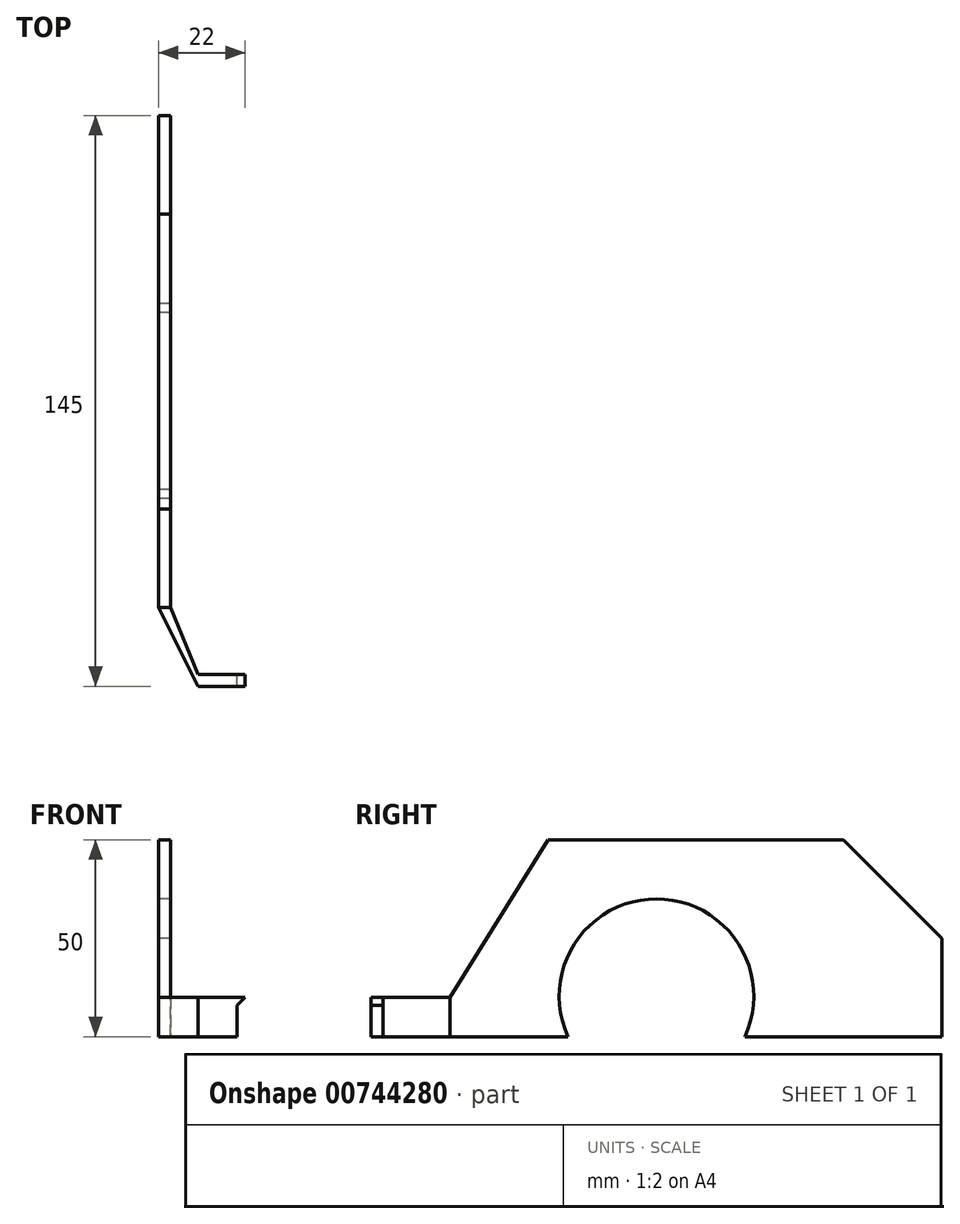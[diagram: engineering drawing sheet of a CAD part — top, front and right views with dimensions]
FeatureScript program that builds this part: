
annotation { "Feature Type Name" : "Feature", "Feature Type Description" : "" }
export const myFeature = defineFeature(function(context is Context, id is Id, definition is map)
    precondition{}
    {
        {
            var Q0;
            Q0=qCreatedBy(makeId("Top.planeOp"),FACE);
            var sketch = newSketch(context, id + "F0", { "sketchPlane" : qUnion([Q0])});
            skLineSegment(sketch, "E0", {"start": v(0, 0) * mm, "end": v(0, 3) * mm});
            skLineSegment(sketch, "E1", {"start": v(0, 3) * mm, "end": v(10, 3) * mm});
            skLineSegment(sketch, "E2", {"start": v(10, 3) * mm, "end": v(17, 20) * mm});
            skLineSegment(sketch, "E3", {"start": v(17, 20) * mm, "end": v(17, 145) * mm});
            skLineSegment(sketch, "E4", {"start": v(17, 145) * mm, "end": v(20, 145) * mm});
            skLineSegment(sketch, "E5", {"start": v(20, 145) * mm, "end": v(20, 20) * mm});
            skLineSegment(sketch, "E6", {"start": v(20, 20) * mm, "end": v(10, 0) * mm});
            skLineSegment(sketch, "E7", {"start": v(10, 0) * mm, "end": v(0, 0) * mm});
            skSolve(sketch);
        }
        {
            var Q0;
            Q0=makeQuery(id+"F0.imprint","IMPRINT",FACE,{"disambiguationData":[TD([[makeQuery(id+"F0.imprint","IMPRINT",EDGE,{"derivedFrom":sQuery(id+"F0.wireOp",EDGE,"E0")}),-1.0]])]});
            extrude(context, id + "F1", {"entities" : qUnion([Q0]), "depth" : 10 * mm, "offsetDistance" : 25 * mm});
        }
        {
            var Q0;
            Q0=qCreatedBy(makeId("Front.planeOp"),FACE);
            var sketch = newSketch(context, id + "F2", { "sketchPlane" : qUnion([Q0])});
            skLineSegment(sketch, "E8", {"start": v(0, 10) * mm, "end": v(-2, 10) * mm});
            skLineSegment(sketch, "E9", {"start": v(-2, 10) * mm, "end": v(0, 8) * mm});
            skLineSegment(sketch, "E10", {"start": v(0, 8) * mm, "end": v(0, 10) * mm});
            skSolve(sketch);
        }
        {
            var Q0;
            Q0=qSketchRegion(id+"F2",true);
            extrude(context, id + "F3", {"entities" : qUnion([Q0]), "operationType" : NewBodyOperationType.ADD, "oppositeDirection" : true, "depth" : 3 * mm, "offsetDistance" : 25 * mm});
        }
        {
            var Q0;
            Q0=makeQuery(id+"F3.boolean.opBoolean","MERGE",FACE,{"derivedFrom":[makeQuery(id+"F1.opExtrude","CAP_FACE",FACE,{"disambiguationData":[OSD([sQuery(id+"F0.wireOp",EDGE,"E0"),sQuery(id+"F0.wireOp",EDGE,"E1"),sQuery(id+"F0.wireOp",EDGE,"E2"),sQuery(id+"F0.wireOp",EDGE,"E3"),sQuery(id+"F0.wireOp",EDGE,"E4"),sQuery(id+"F0.wireOp",EDGE,"E5"),sQuery(id+"F0.wireOp",EDGE,"E6"),sQuery(id+"F0.wireOp",EDGE,"E7")])],"isStart":false}),makeQuery(id+"F3.opExtrude","SWEPT_FACE",FACE,{"disambiguationData":[OSD([sQuery(id+"F2.wireOp",EDGE,"E8")])]})]});
            var sketch = newSketch(context, id + "F4", { "sketchPlane" : qUnion([Q0])});
            skLineSegment(sketch, "E11.bottom", {"start": v(20, 20) * mm, "end": v(17, 20) * mm});
            skLineSegment(sketch, "E11.top", {"start": v(20, 145) * mm, "end": v(17, 145) * mm});
            skLineSegment(sketch, "E11.left", {"start": v(20, 20) * mm, "end": v(20, 145) * mm});
            skLineSegment(sketch, "E11.right", {"start": v(17, 20) * mm, "end": v(17, 145) * mm});
            skSolve(sketch);
        }
        {
            var Q0;
            Q0=qSketchRegion(id+"F4",true);
            extrude(context, id + "F5", {"entities" : qUnion([Q0]), "operationType" : NewBodyOperationType.ADD, "depth" : 40 * mm, "offsetDistance" : 25 * mm});
        }
        {
            var Q0;
            Q0=makeQuery(id+"F5.opExtrude","CAP_EDGE",EDGE,{"disambiguationData":[OSD([sQuery(id+"F4.wireOp",EDGE,"E11.bottom")])],"isStart":false});
            chamfer(context, id + "F6", {"entities" : qUnion([Q0]), "chamferType" : ChamferType.TWO_OFFSETS, "width1" : 40 * mm, "oppositeDirection" : false, "width2" : 25 * mm, "tangentPropagation" : true});
        }
        {
            var Q0;
            Q0=makeQuery(id+"F5.opExtrude","CAP_EDGE",EDGE,{"disambiguationData":[OSD([sQuery(id+"F4.wireOp",EDGE,"E11.top")])],"isStart":false});
            chamfer(context, id + "F7", {"entities" : qUnion([Q0]), "width" : 25 * mm, "tangentPropagation" : true});
        }
        {
            var Q0;
            Q0=makeQuery(id+"F5.boolean.opBoolean","MERGE",FACE,{"derivedFrom":[makeQuery(id+"F1.opExtrude","SWEPT_FACE",FACE,{"disambiguationData":[OSD([sQuery(id+"F0.wireOp",EDGE,"E5")])]}),makeQuery(id+"F5.opExtrude","SWEPT_FACE",FACE,{"disambiguationData":[OSD([sQuery(id+"F4.wireOp",EDGE,"E11.left")])]})]});
            var sketch = newSketch(context, id + "F8", { "sketchPlane" : qUnion([Q0])});
            skArc(sketch, "E12", {"start": v(95, 0) * mm, "mid": v(72.5, 35) * mm, "end": v(50, 0) * mm});
            skSolve(sketch);
        }
        {
            var Q0;
            {var subQ0=sQuery(id+"F8.wireOp",EDGE,"E12");Q0=makeQuery(id+"F8.imprint","IMPRINT",FACE,{"disambiguationData":[TD([[makeQuery(id+"F8.imprint","IMPRINT",EDGE,{"derivedFrom":subQ0}),1.0]])]});}
            extrude(context, id + "F9", {"entities" : qUnion([Q0]), "operationType" : NewBodyOperationType.REMOVE, "oppositeDirection" : true, "depth" : 25 * mm, "offsetDistance" : 25 * mm});
        }
        {
            var Q0;
            Q0=qCreatedBy(makeId("Right.planeOp"),FACE);
            cPlane(context, id + "F10", {"entities" : qUnion([Q0]), "cplaneType" : CPlaneType.OFFSET, "offset" : 2 * mm, "oppositeDirection" : true, "width" : 150 * mm, "height" : 150 * mm});
        }
        {
            var Q0;
            Q0=makeQuery(id+"F1.opExtrude","SWEPT_BODY",BODY,{"disambiguationData":[OSD([sQuery(id+"F0.wireOp",EDGE,"E0"),sQuery(id+"F0.wireOp",EDGE,"E1"),sQuery(id+"F0.wireOp",EDGE,"E2"),sQuery(id+"F0.wireOp",EDGE,"E3"),sQuery(id+"F0.wireOp",EDGE,"E4"),sQuery(id+"F0.wireOp",EDGE,"E5"),sQuery(id+"F0.wireOp",EDGE,"E6"),sQuery(id+"F0.wireOp",EDGE,"E7")])]});
            var Q1;
            Q1=qCreatedBy(id+"F10.planeOp",FACE);
            mirror(context, id + "F11", {"entities" : qUnion([Q0]), "mirrorPlane" : qUnion([Q1])});
        }
        {
            var Q0;
            Q0=makeQuery(id+"F1.opExtrude","SWEPT_BODY",BODY,{"disambiguationData":[OSD([sQuery(id+"F0.wireOp",EDGE,"E0"),sQuery(id+"F0.wireOp",EDGE,"E1"),sQuery(id+"F0.wireOp",EDGE,"E2"),sQuery(id+"F0.wireOp",EDGE,"E3"),sQuery(id+"F0.wireOp",EDGE,"E4"),sQuery(id+"F0.wireOp",EDGE,"E5"),sQuery(id+"F0.wireOp",EDGE,"E6"),sQuery(id+"F0.wireOp",EDGE,"E7")])]});
            deleteBodies(context, id + "F12", {"entities" : qUnion([Q0])});
        }
    });
